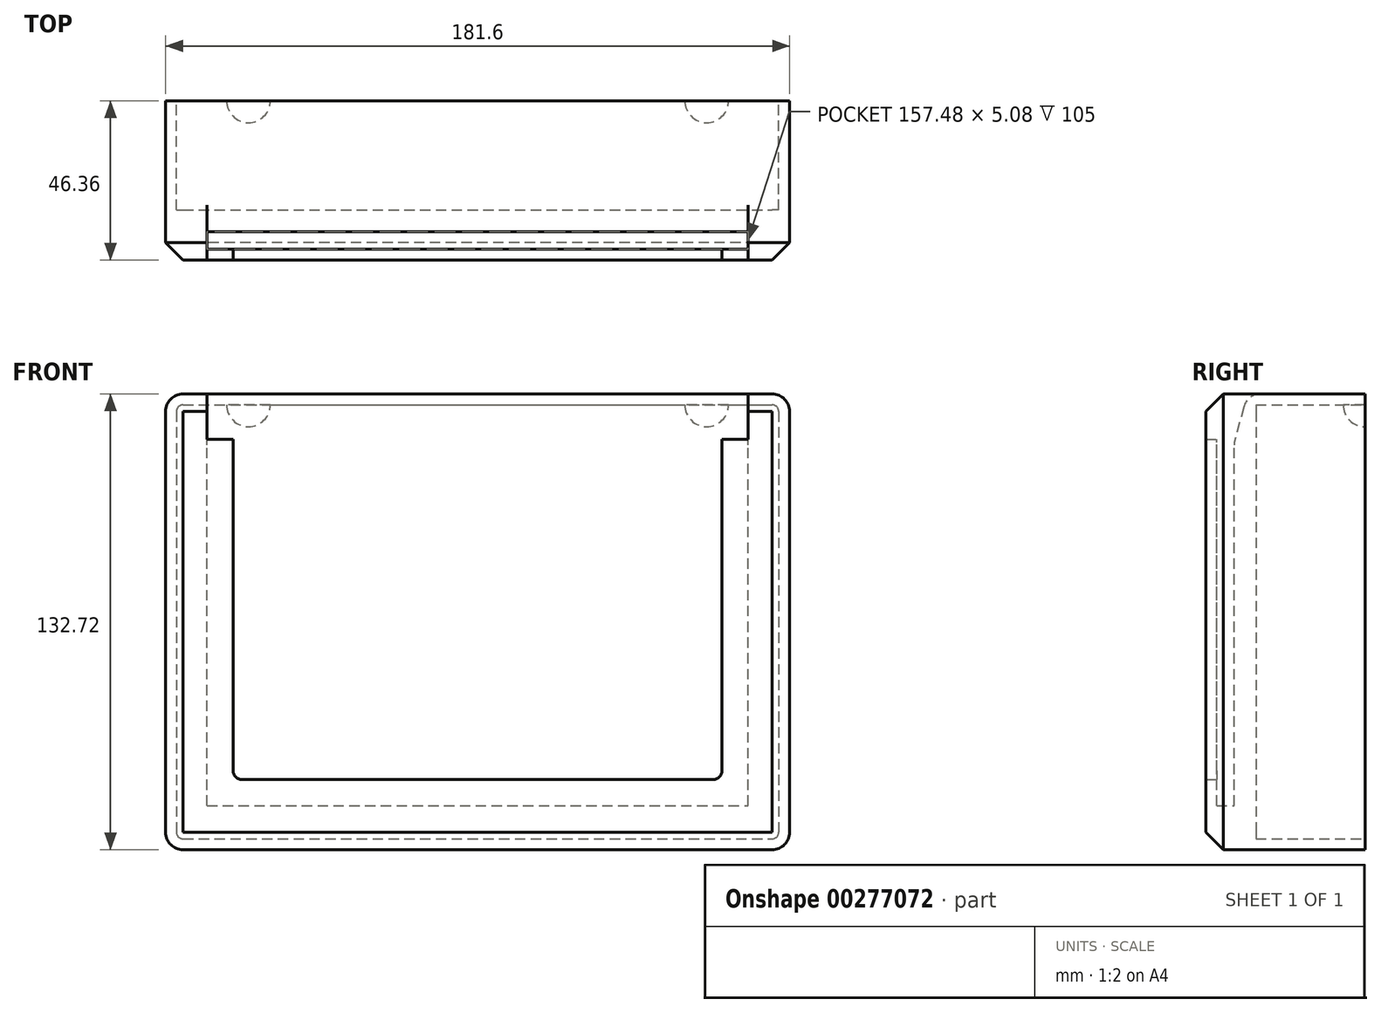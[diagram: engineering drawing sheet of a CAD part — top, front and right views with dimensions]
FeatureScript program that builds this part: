
annotation { "Feature Type Name" : "Feature", "Feature Type Description" : "" }
export const myFeature = defineFeature(function(context is Context, id is Id, definition is map)
    precondition{}
    {
        {
            var Q0;
            Q0=qCreatedBy(makeId("Front.planeOp"),FACE);
            var sketch = newSketch(context, id + "F0", { "sketchPlane" : qUnion([Q0])});
            skLineSegment(sketch, "E0.bottom", {"start": v(-84.45, 58.42) * mm, "end": v(84.46, 58.42) * mm, "construction": true});
            skLineSegment(sketch, "E0.top", {"start": v(-84.46, -58.42) * mm, "end": v(84.45, -58.42) * mm, "construction": true});
            skLineSegment(sketch, "E0.left", {"start": v(-84.45, 58.42) * mm, "end": v(-84.46, -58.42) * mm, "construction": true});
            skLineSegment(sketch, "E0.right", {"start": v(84.46, 58.42) * mm, "end": v(84.45, -58.42) * mm, "construction": true});
            skPoint(sketch, "E0.middle", {"position": v(0, 0) * mm});
            skLineSegment(sketch, "E1.0", {"start": v(-90.8, 64.77) * mm, "end": v(90.8, 64.77) * mm});
            skLineSegment(sketch, "E1.1", {"start": v(-90.8, 64.77) * mm, "end": v(-90.8, -67.94) * mm});
            skLineSegment(sketch, "E1.3", {"start": v(90.8, 64.77) * mm, "end": v(90.8, -67.94) * mm});
            skLineSegment(sketch, "E2.0", {"start": v(-90.8, -67.94) * mm, "end": v(90.8, -67.94) * mm});
            skSolve(sketch);
        }
        {
            var Q0;
            Q0 = qSketchRegion(id + "F0", true);
            extrude(context, id + "F1", {"entities" : qUnion([Q0]), "offsetDistance" : 25.4 * mm, "depth" : 34.92 * mm});
        }
        {
            var Q0;
            Q0=makeQuery(id+"F1.opExtrude","SWEPT_EDGE",EDGE,{"disambiguationData":[OSD([sQuery(id+"F0.wireOp",EDGE,"E1.0"),sQuery(id+"F0.wireOp",EDGE,"E1.3")])]});
            var Q1;
            Q1=makeQuery(id+"F1.opExtrude","SWEPT_EDGE",EDGE,{"disambiguationData":[OSD([sQuery(id+"F0.wireOp",EDGE,"E1.0"),sQuery(id+"F0.wireOp",EDGE,"E1.1")])]});
            var Q2;
            Q2=makeQuery(id+"F1.opExtrude","SWEPT_EDGE",EDGE,{"disambiguationData":[OSD([sQuery(id+"F0.wireOp",EDGE,"E1.1"),sQuery(id+"F0.wireOp",EDGE,"E1.2")])]});
            var Q3;
            Q3=makeQuery(id+"F1.opExtrude","SWEPT_EDGE",EDGE,{"disambiguationData":[OSD([sQuery(id+"F0.wireOp",EDGE,"E1.2"),sQuery(id+"F0.wireOp",EDGE,"E1.3")])]});
            fillet(context, id + "F2", {"entities" : qUnion([Q0, Q1, Q2, Q3]), "radius" : 5.08 * mm, "tangentPropagation" : true, "allowEdgeOverflow" : false});
        }
        {
            var Q0;
            Q0=makeQuery(id+"F1.opExtrude","CAP_FACE",FACE,{"disambiguationData":[OSD([sQuery(id+"F0.wireOp",EDGE,"E1.0"),sQuery(id+"F0.wireOp",EDGE,"E1.1"),sQuery(id+"F0.wireOp",EDGE,"E1.2"),sQuery(id+"F0.wireOp",EDGE,"E1.3")])],"isStart":true});
            shell(context, id + "F3", {"entities" : qUnion([Q0]), "thickness" : 3.17 * mm});
        }
        {
            var Q0;
            Q0=makeQuery(id+"F1.opExtrude","CAP_FACE",FACE,{"disambiguationData":[OSD([sQuery(id+"F0.wireOp",EDGE,"E1.0"),sQuery(id+"F0.wireOp",EDGE,"E1.1"),sQuery(id+"F0.wireOp",EDGE,"E1.3"),sQuery(id+"F0.wireOp",EDGE,"E2.0")])],"isStart":false});
            extrude(context, id + "F4", {"entities" : qUnion([Q0]), "operationType" : NewBodyOperationType.ADD, "depth" : 3.17 * mm});
        }
        {
            var Q0;
            Q0=makeQuery(id+"F3.opShell","OFFSET_FACE",FACE,{"disambiguationData":[OSD([sQuery(id+"F0.wireOp",EDGE,"E1.0")])]});
            var sketch = newSketch(context, id + "F5", { "sketchPlane" : qUnion([Q0])});
            skArc(sketch, "E3", {"start": v(-60.33, 0) * mm, "mid": v(-66.68, 6.35) * mm, "end": v(-73.03, 0) * mm});
            skLineSegment(sketch, "E4.0", {"start": v(-73.03, 0) * mm, "end": v(-60.33, 0) * mm});
            skPoint(sketch, "E5.orphan", {"position": v(-85.73, 0) * mm});
            skPoint(sketch, "E6.orphan", {"position": v(85.73, 0) * mm});
            skArc(sketch, "E7", {"start": v(73.03, 0) * mm, "mid": v(66.68, 6.35) * mm, "end": v(60.33, 0) * mm});
            skLineSegment(sketch, "E8", {"start": v(60.33, 0) * mm, "end": v(73.03, 0) * mm});
            skSolve(sketch);
        }
        {
            var Q0;
            Q0=makeQuery(id+"F5.imprint","IMPRINT",FACE,{"disambiguationData":[TD([[makeQuery(id+"F5.imprint","IMPRINT",EDGE,{"derivedFrom":sQuery(id+"F5.wireOp",EDGE,"E3")}),1.0]])]});
            var Q1;
            Q1=makeQuery(id+"F5.imprint","IMPRINT",FACE,{"disambiguationData":[TD([[makeQuery(id+"F5.imprint","IMPRINT",EDGE,{"derivedFrom":sQuery(id+"F5.wireOp",EDGE,"E7")}),1.0]])]});
            var Q2;
            {var subQ0=sQuery(id+"F0.wireOp",EDGE,"E1.0");Q2=makeQuery(id+"F3.opShell","OFFSET_EDGE",EDGE,{"disambiguationData":[OSD([subQ0]),TDD([makeQuery(id+"F1.opExtrude","CAP_EDGE",EDGE,{"disambiguationData":[OSD([subQ0])],"isStart":true})])]});}
            revolve(context, id + "F6", {"operationType" : NewBodyOperationType.ADD, "entities" : qUnion([Q0, Q1]), "axis" : qUnion([Q2]), "revolveType" : RevolveType.ONE_DIRECTION, "angle" : 90 * degree});
        }
        {
            var Q0;
            Q0=makeQuery(id+"F4.opExtrude","CAP_FACE",FACE,{"disambiguationData":[OSD([sQuery(id+"F0.wireOp",EDGE,"E1.0"),sQuery(id+"F0.wireOp",EDGE,"E1.1"),sQuery(id+"F0.wireOp",EDGE,"E1.3"),sQuery(id+"F0.wireOp",EDGE,"E2.0")])],"isStart":false});
            var sketch = newSketch(context, id + "F7", { "sketchPlane" : qUnion([Q0])});
            skLineSegment(sketch, "E9.bottom", {"start": v(-78.74, -55.12) * mm, "end": v(78.74, -55.12) * mm});
            skLineSegment(sketch, "E9.left", {"start": v(-78.74, -55.12) * mm, "end": v(-78.74, 51.56) * mm});
            skLineSegment(sketch, "E9.right", {"start": v(78.74, -55.12) * mm, "end": v(78.74, 51.56) * mm});
            skPoint(sketch, "E9.middle", {"position": v(0, -1.78) * mm});
            skLineSegment(sketch, "E10.0", {"start": v(-81.92, -58.3) * mm, "end": v(-81.92, 51.56) * mm});
            skLineSegment(sketch, "E10.1", {"start": v(-81.91, -58.3) * mm, "end": v(81.92, -58.3) * mm});
            skLineSegment(sketch, "E10.2", {"start": v(81.92, -58.3) * mm, "end": v(81.92, 51.56) * mm});
            skLineSegment(sketch, "E11", {"start": v(-81.92, 51.56) * mm, "end": v(-78.74, 51.56) * mm});
            skLineSegment(sketch, "E12", {"start": v(78.74, 51.56) * mm, "end": v(81.92, 51.56) * mm});
            skLineSegment(sketch, "E13.bottom", {"start": v(-76.2, 49.02) * mm, "end": v(76.2, 49.02) * mm, "construction": true});
            skLineSegment(sketch, "E13.top", {"start": v(-76.2, -52.58) * mm, "end": v(76.2, -52.58) * mm, "construction": true});
            skLineSegment(sketch, "E13.left", {"start": v(-76.2, 49.02) * mm, "end": v(-76.2, -52.58) * mm, "construction": true});
            skLineSegment(sketch, "E13.right", {"start": v(76.2, 49.02) * mm, "end": v(76.2, -52.58) * mm, "construction": true});
            skSolve(sketch);
        }
        {
            var Q0;
            Q0 = qSketchRegion(id + "F7", true);
            extrude(context, id + "F8", {"entities" : qUnion([Q0]), "operationType" : NewBodyOperationType.ADD, "depth" : 5.08 * mm, "offsetDistance" : 25.4 * mm});
        }
        {
            var Q0;
            Q0=makeQuery(id+"F8.opExtrude","CAP_FACE",FACE,{"disambiguationData":[OSD([sQuery(id+"F7.wireOp",EDGE,"E9.bottom"),sQuery(id+"F7.wireOp",EDGE,"E9.left"),sQuery(id+"F7.wireOp",EDGE,"E9.right"),sQuery(id+"F7.wireOp",EDGE,"E10.0"),sQuery(id+"F7.wireOp",EDGE,"E10.1"),sQuery(id+"F7.wireOp",EDGE,"E10.2"),sQuery(id+"F7.wireOp",EDGE,"E11"),sQuery(id+"F7.wireOp",EDGE,"E12")])],"isStart":false});
            var sketch = newSketch(context, id + "F9", { "sketchPlane" : qUnion([Q0])});
            skLineSegment(sketch, "E14.0", {"start": v(-81.92, -58.3) * mm, "end": v(-81.92, 51.56) * mm});
            skLineSegment(sketch, "E15.0", {"start": v(-81.91, -58.3) * mm, "end": v(81.92, -58.3) * mm});
            skLineSegment(sketch, "E16.0", {"start": v(81.92, -58.3) * mm, "end": v(81.92, 51.56) * mm});
            skLineSegment(sketch, "E17.0", {"start": v(-71.12, -47.5) * mm, "end": v(-71.12, 51.56) * mm});
            skLineSegment(sketch, "E17.1", {"start": v(-71.12, -47.5) * mm, "end": v(71.12, -47.5) * mm});
            skLineSegment(sketch, "E17.2", {"start": v(71.12, -47.5) * mm, "end": v(71.12, 51.56) * mm});
            skLineSegment(sketch, "E18", {"start": v(-81.92, 51.56) * mm, "end": v(-71.12, 51.56) * mm});
            skLineSegment(sketch, "E19", {"start": v(71.12, 51.56) * mm, "end": v(81.92, 51.56) * mm});
            skSolve(sketch);
        }
        {
            var Q0;
            Q0 = qSketchRegion(id + "F9", true);
            extrude(context, id + "F10", {"entities" : qUnion([Q0]), "operationType" : NewBodyOperationType.ADD, "depth" : 3.17 * mm, "offsetDistance" : 25.4 * mm});
        }
        {
            var Q0;
            Q0=makeQuery(id+"F4.opExtrude","CAP_FACE",FACE,{"disambiguationData":[OSD([sQuery(id+"F0.wireOp",EDGE,"E1.0"),sQuery(id+"F0.wireOp",EDGE,"E1.1"),sQuery(id+"F0.wireOp",EDGE,"E1.3"),sQuery(id+"F0.wireOp",EDGE,"E2.0")])],"isStart":false});
            var sketch = newSketch(context, id + "F11", { "sketchPlane" : qUnion([Q0])});
            skLineSegment(sketch, "E20.0.0", {"start": v(-90.8, 59.69) * mm, "end": v(-90.8, -62.86) * mm});
            skArc(sketch, "E20.0.1", {"start": v(-90.8, -62.86) * mm, "mid": v(-89.32, -66.46) * mm, "end": v(-85.73, -67.94) * mm});
            skLineSegment(sketch, "E20.0.2", {"start": v(-85.73, -67.94) * mm, "end": v(85.73, -67.94) * mm});
            skArc(sketch, "E20.0.3", {"start": v(85.73, -67.94) * mm, "mid": v(89.32, -66.46) * mm, "end": v(90.8, -62.86) * mm});
            skLineSegment(sketch, "E20.0.4", {"start": v(90.8, -62.86) * mm, "end": v(90.8, 59.69) * mm});
            skArc(sketch, "E20.0.5", {"start": v(90.8, 59.69) * mm, "mid": v(89.32, 63.28) * mm, "end": v(85.73, 64.77) * mm});
            skLineSegment(sketch, "E20.0.6", {"start": v(85.73, 64.77) * mm, "end": v(81.92, 64.77) * mm});
            skArc(sketch, "E20.0.7", {"start": v(-85.73, 64.77) * mm, "mid": v(-89.32, 63.28) * mm, "end": v(-90.8, 59.69) * mm});
            skLineSegment(sketch, "E21.0.5", {"start": v(-81.92, 51.56) * mm, "end": v(-81.92, -58.3) * mm});
            skLineSegment(sketch, "E21.0.6", {"start": v(-81.91, -58.3) * mm, "end": v(81.92, -58.3) * mm});
            skLineSegment(sketch, "E21.0.7", {"start": v(81.92, -58.3) * mm, "end": v(81.92, 51.56) * mm});
            skLineSegment(sketch, "E22", {"start": v(-81.92, 51.56) * mm, "end": v(-81.92, 64.77) * mm});
            skLineSegment(sketch, "E23", {"start": v(81.92, 51.56) * mm, "end": v(81.92, 64.77) * mm});
            skLineSegment(sketch, "E24.trimOffspring", {"start": v(-81.91, 64.77) * mm, "end": v(-85.73, 64.77) * mm});
            skLineSegment(sketch, "E25.bottom", {"start": v(-78.74, 51.56) * mm, "end": v(-81.92, 51.56) * mm});
            skLineSegment(sketch, "E25.top", {"start": v(-78.74, 64.77) * mm, "end": v(-81.92, 64.77) * mm});
            skLineSegment(sketch, "E25.left", {"start": v(-78.74, 51.56) * mm, "end": v(-78.74, 64.77) * mm});
            skLineSegment(sketch, "E25.right", {"start": v(-81.92, 51.56) * mm, "end": v(-81.92, 64.77) * mm, "construction": true});
            skLineSegment(sketch, "E26.bottom", {"start": v(78.74, 51.56) * mm, "end": v(81.92, 51.56) * mm});
            skLineSegment(sketch, "E26.top", {"start": v(78.74, 64.77) * mm, "end": v(81.92, 64.77) * mm});
            skLineSegment(sketch, "E26.left", {"start": v(78.74, 51.56) * mm, "end": v(78.74, 64.77) * mm});
            skLineSegment(sketch, "E26.right", {"start": v(81.92, 51.56) * mm, "end": v(81.92, 64.77) * mm, "construction": true});
            skSolve(sketch);
        }
        {
            var Q0;
            Q0 = qSketchRegion(id + "F11", true);
            var Q1;
            Q1=makeQuery(id+"F10.opExtrude","CAP_FACE",FACE,{"disambiguationData":[OSD([sQuery(id+"F9.wireOp",EDGE,"E14.0"),sQuery(id+"F9.wireOp",EDGE,"E15.0"),sQuery(id+"F9.wireOp",EDGE,"E16.0"),sQuery(id+"F9.wireOp",EDGE,"E17.0"),sQuery(id+"F9.wireOp",EDGE,"E17.1"),sQuery(id+"F9.wireOp",EDGE,"E17.2"),sQuery(id+"F9.wireOp",EDGE,"E18"),sQuery(id+"F9.wireOp",EDGE,"E19")])],"isStart":false});
            extrude(context, id + "F12", {"entities" : qUnion([Q0]), "operationType" : NewBodyOperationType.ADD, "endBound" : BoundingType.UP_TO_SURFACE, "depth" : 25.4 * mm, "endBoundEntityFace" : qUnion([Q1]), "offsetDistance" : 25.4 * mm});
        }
        {
            var Q0;
            Q0=makeQuery(id+"F12.opExtrude","CAP_EDGE",EDGE,{"disambiguationData":[OSD([sQuery(id+"F11.wireOp",EDGE,"E20.0.4")])],"isStart":false});
            chamfer(context, id + "F13", {"entities" : qUnion([Q0]), "width" : 5.08 * mm, "tangentPropagation" : true});
        }
        {
            var Q0;
            Q0=makeQuery(id+"F4.opExtrude","CAP_EDGE",EDGE,{"disambiguationData":[OSD([sQuery(id+"F0.wireOp",EDGE,"E1.0")])],"isStart":false});
            chamfer(context, id + "F14", {"entities" : qUnion([Q0]), "chamferType" : ChamferType.OFFSET_ANGLE, "width" : 3.8 * mm, "oppositeDirection" : false, "angle" : 75 * degree, "tangentPropagation" : true});
        }
        {
            var Q0;
            Q0=makeQuery(id+"F10.opExtrude","SWEPT_EDGE",EDGE,{"disambiguationData":[OSD([sQuery(id+"F9.wireOp",EDGE,"E17.0"),sQuery(id+"F9.wireOp",EDGE,"E17.1")])]});
            var Q1;
            Q1=makeQuery(id+"F10.opExtrude","SWEPT_EDGE",EDGE,{"disambiguationData":[OSD([sQuery(id+"F9.wireOp",EDGE,"E17.1"),sQuery(id+"F9.wireOp",EDGE,"E17.2")])]});
            var Q2;
            Q2=makeQuery(id+"F15.opExtrude","SWEPT_EDGE",EDGE,{"disambiguationData":[OSD([sQuery(id+"F9iZdTMr8qaSHOt_1.wireOp",EDGE,"Y4VOi2jY-tBfe-8jJB-qcHL-p3kgb7XRAiGI.bottom"),sQuery(id+"F9iZdTMr8qaSHOt_1.wireOp",EDGE,"Y4VOi2jY-tBfe-8jJB-qcHL-p3kgb7XRAiGI.right")])]});
            var Q3;
            Q3=makeQuery(id+"F15.opExtrude","SWEPT_EDGE",EDGE,{"disambiguationData":[OSD([sQuery(id+"F9iZdTMr8qaSHOt_1.wireOp",EDGE,"PYTGcFao-uGwc-9iIK-wDhJ-kfCVSGKSmMZ3.bottom"),sQuery(id+"F9iZdTMr8qaSHOt_1.wireOp",EDGE,"PYTGcFao-uGwc-9iIK-wDhJ-kfCVSGKSmMZ3.right")])]});
            fillet(context, id + "F16", {"entities" : qUnion([Q0, Q1, Q2, Q3]), "radius" : 2.54 * mm, "tangentPropagation" : true, "allowEdgeOverflow" : false});
        }
        {
            var Q0;
            {var subQ0=sQuery(id+"F0.wireOp",EDGE,"E1.0");Q0=makeQuery(id+"F14.opChamfer","BLEND_EDGE",EDGE,{"blendedFrom":[makeQuery(id+"F4.opExtrude","CAP_EDGE",EDGE,{"disambiguationData":[OSD([subQ0])],"isStart":false}),makeQuery(id+"F12.boolean.opBoolean","MERGE",FACE,{"derivedFrom":[makeQuery(id+"F4.boolean.opBoolean","MERGE",FACE,{"derivedFrom":[makeQuery(id+"F1.opExtrude","SWEPT_FACE",FACE,{"disambiguationData":[OSD([subQ0])]}),makeQuery(id+"F4.opExtrude","SWEPT_FACE",FACE,{"disambiguationData":[OSD([subQ0])]})]}),makeQuery(id+"F12.opExtrude","SWEPT_FACE",FACE,{"disambiguationData":[OSD([sQuery(id+"F11.wireOp",EDGE,"E20.0.6"),sQuery(id+"F11.wireOp",EDGE,"E26.top")])]}),makeQuery(id+"F12.opExtrude","SWEPT_FACE",FACE,{"disambiguationData":[OSD([sQuery(id+"F11.wireOp",EDGE,"E24.trimOffspring"),sQuery(id+"F11.wireOp",EDGE,"E25.top")])]})]})],"blendedInto":[makeQuery(id+"F12.boolean.opBoolean","MERGE",FACE,{"derivedFrom":[makeQuery(id+"F4.boolean.opBoolean","MERGE",FACE,{"derivedFrom":[makeQuery(id+"F1.opExtrude","SWEPT_FACE",FACE,{"disambiguationData":[OSD([subQ0])]}),makeQuery(id+"F4.opExtrude","SWEPT_FACE",FACE,{"disambiguationData":[OSD([subQ0])]})]}),makeQuery(id+"F12.opExtrude","SWEPT_FACE",FACE,{"disambiguationData":[OSD([sQuery(id+"F11.wireOp",EDGE,"E20.0.6"),sQuery(id+"F11.wireOp",EDGE,"E26.top")])]}),makeQuery(id+"F12.opExtrude","SWEPT_FACE",FACE,{"disambiguationData":[OSD([sQuery(id+"F11.wireOp",EDGE,"E24.trimOffspring"),sQuery(id+"F11.wireOp",EDGE,"E25.top")])]})]})]});}
            var Q1;
            {var subQ0=sQuery(id+"F0.wireOp",EDGE,"E1.0");Q1=makeQuery(id+"F14.opChamfer","BLEND_EDGE",EDGE,{"blendedFrom":[makeQuery(id+"F4.opExtrude","CAP_EDGE",EDGE,{"disambiguationData":[OSD([subQ0])],"isStart":false}),makeQuery(id+"F4.opExtrude","CAP_FACE",FACE,{"disambiguationData":[OSD([subQ0,sQuery(id+"F0.wireOp",EDGE,"E1.1"),sQuery(id+"F0.wireOp",EDGE,"E1.3"),sQuery(id+"F0.wireOp",EDGE,"E2.0")])],"isStart":false})],"blendedInto":[makeQuery(id+"F4.opExtrude","CAP_FACE",FACE,{"disambiguationData":[OSD([subQ0,sQuery(id+"F0.wireOp",EDGE,"E1.1"),sQuery(id+"F0.wireOp",EDGE,"E1.3"),sQuery(id+"F0.wireOp",EDGE,"E2.0")])],"isStart":false})]});}
            fillet(context, id + "F17", {"entities" : qUnion([Q0, Q1]), "radius" : 5.08 * mm, "tangentPropagation" : true, "allowEdgeOverflow" : false});
        }
    });
